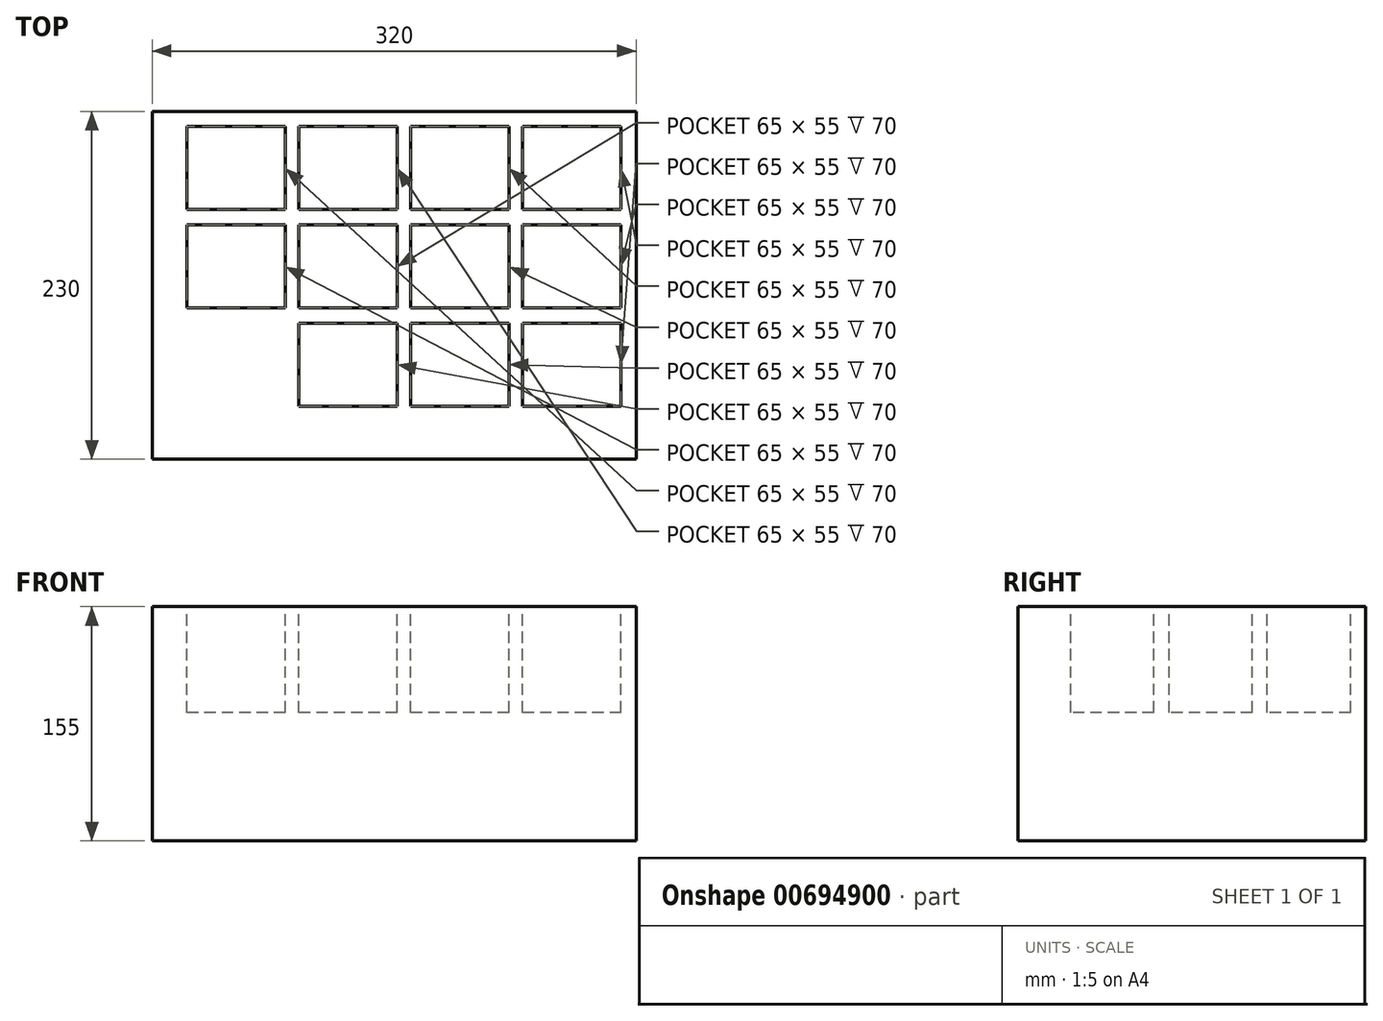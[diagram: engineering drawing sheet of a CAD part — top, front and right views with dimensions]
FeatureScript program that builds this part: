
annotation { "Feature Type Name" : "Feature", "Feature Type Description" : "" }
export const myFeature = defineFeature(function(context is Context, id is Id, definition is map)
    precondition{}
    {
        {
            var Q0;
            Q0=qCreatedBy(makeId("Top.planeOp"),FACE);
            var sketch = newSketch(context, id + "F0", { "sketchPlane" : qUnion([Q0])});
            skLineSegment(sketch, "E0.bottom", {"start": v(0, 0) * mm, "end": v(320, 0) * mm});
            skLineSegment(sketch, "E0.top", {"start": v(0, 230) * mm, "end": v(320, 230) * mm});
            skLineSegment(sketch, "E0.left", {"start": v(0, 0) * mm, "end": v(0, 230) * mm});
            skLineSegment(sketch, "E0.right", {"start": v(320, 0) * mm, "end": v(320, 230) * mm});
            skSolve(sketch);
        }
        {
            var Q0;
            Q0=makeQuery(id+"F0.imprint","IMPRINT",FACE,{"disambiguationData":[TD([[makeQuery(id+"F0.imprint","IMPRINT",EDGE,{"derivedFrom":sQuery(id+"F0.wireOp",EDGE,"E0.bottom")}),1.0]])]});
            extrude(context, id + "F1", {"entities" : qUnion([Q0]), "depth" : 155 * mm, "offsetDistance" : 25 * mm});
        }
        {
            var Q0;
            Q0=makeQuery(id+"F1.opExtrude","CAP_FACE",FACE,{"disambiguationData":[OSD([sQuery(id+"F0.wireOp",EDGE,"E0.bottom"),sQuery(id+"F0.wireOp",EDGE,"E0.top"),sQuery(id+"F0.wireOp",EDGE,"E0.left"),sQuery(id+"F0.wireOp",EDGE,"E0.right")])],"isStart":false});
            var sketch = newSketch(context, id + "F2", { "sketchPlane" : qUnion([Q0])});
            skLineSegment(sketch, "E1.bottom", {"start": v(320, 230) * mm, "end": v(310, 230) * mm});
            skLineSegment(sketch, "E1.top", {"start": v(320, 220) * mm, "end": v(310, 220) * mm});
            skLineSegment(sketch, "E1.left", {"start": v(320, 230) * mm, "end": v(320, 220) * mm});
            skLineSegment(sketch, "E1.right", {"start": v(310, 230) * mm, "end": v(310, 220) * mm});
            skLineSegment(sketch, "E2.bottom", {"start": v(310, 220) * mm, "end": v(245, 220) * mm});
            skLineSegment(sketch, "E2.top", {"start": v(310, 165) * mm, "end": v(245, 165) * mm});
            skLineSegment(sketch, "E2.left", {"start": v(310, 220) * mm, "end": v(310, 165) * mm});
            skLineSegment(sketch, "E2.right", {"start": v(245, 220) * mm, "end": v(245, 165) * mm});
            skLineSegment(sketch, "E3.0.1.0", {"start": v(310, 155) * mm, "end": v(245, 155) * mm});
            skLineSegment(sketch, "E3.0.1.1", {"start": v(245, 155) * mm, "end": v(245, 100) * mm});
            skLineSegment(sketch, "E3.0.1.2", {"start": v(310, 155) * mm, "end": v(310, 100) * mm});
            skLineSegment(sketch, "E3.0.1.3", {"start": v(310, 100) * mm, "end": v(245, 100) * mm});
            skLineSegment(sketch, "E3.0.2.0", {"start": v(310, 90) * mm, "end": v(245, 90) * mm});
            skLineSegment(sketch, "E3.0.2.1", {"start": v(245, 90) * mm, "end": v(245, 35) * mm});
            skLineSegment(sketch, "E3.0.2.2", {"start": v(310, 90) * mm, "end": v(310, 35) * mm});
            skLineSegment(sketch, "E3.0.2.3", {"start": v(310, 35) * mm, "end": v(245, 35) * mm});
            skLineSegment(sketch, "E3.1.0.0", {"start": v(236, 220) * mm, "end": v(171, 220) * mm});
            skLineSegment(sketch, "E3.1.0.1", {"start": v(171, 220) * mm, "end": v(171, 165) * mm});
            skLineSegment(sketch, "E3.1.0.2", {"start": v(236, 220) * mm, "end": v(236, 165) * mm});
            skLineSegment(sketch, "E3.1.0.3", {"start": v(236, 165) * mm, "end": v(171, 165) * mm});
            skLineSegment(sketch, "E3.1.1.0", {"start": v(236, 155) * mm, "end": v(171, 155) * mm});
            skLineSegment(sketch, "E3.1.1.1", {"start": v(171, 155) * mm, "end": v(171, 100) * mm});
            skLineSegment(sketch, "E3.1.1.2", {"start": v(236, 155) * mm, "end": v(236, 100) * mm});
            skLineSegment(sketch, "E3.1.1.3", {"start": v(236, 100) * mm, "end": v(171, 100) * mm});
            skLineSegment(sketch, "E3.1.2.0", {"start": v(236, 90) * mm, "end": v(171, 90) * mm});
            skLineSegment(sketch, "E3.1.2.1", {"start": v(171, 90) * mm, "end": v(171, 35) * mm});
            skLineSegment(sketch, "E3.1.2.2", {"start": v(236, 90) * mm, "end": v(236, 35) * mm});
            skLineSegment(sketch, "E3.1.2.3", {"start": v(236, 35) * mm, "end": v(171, 35) * mm});
            skLineSegment(sketch, "E3.2.0.0", {"start": v(162, 220) * mm, "end": v(97, 220) * mm});
            skLineSegment(sketch, "E3.2.0.1", {"start": v(97, 220) * mm, "end": v(97, 165) * mm});
            skLineSegment(sketch, "E3.2.0.2", {"start": v(162, 220) * mm, "end": v(162, 165) * mm});
            skLineSegment(sketch, "E3.2.0.3", {"start": v(162, 165) * mm, "end": v(97, 165) * mm});
            skLineSegment(sketch, "E3.2.1.0", {"start": v(162, 155) * mm, "end": v(97, 155) * mm});
            skLineSegment(sketch, "E3.2.1.1", {"start": v(97, 155) * mm, "end": v(97, 100) * mm});
            skLineSegment(sketch, "E3.2.1.2", {"start": v(162, 155) * mm, "end": v(162, 100) * mm});
            skLineSegment(sketch, "E3.2.1.3", {"start": v(162, 100) * mm, "end": v(97, 100) * mm});
            skLineSegment(sketch, "E3.2.2.0", {"start": v(162, 90) * mm, "end": v(97, 90) * mm});
            skLineSegment(sketch, "E3.2.2.1", {"start": v(97, 90) * mm, "end": v(97, 35) * mm});
            skLineSegment(sketch, "E3.2.2.2", {"start": v(162, 90) * mm, "end": v(162, 35) * mm});
            skLineSegment(sketch, "E3.2.2.3", {"start": v(162, 35) * mm, "end": v(97, 35) * mm});
            skLineSegment(sketch, "E3.3.0.0", {"start": v(88, 220) * mm, "end": v(23, 220) * mm});
            skLineSegment(sketch, "E3.3.0.1", {"start": v(23, 220) * mm, "end": v(23, 165) * mm});
            skLineSegment(sketch, "E3.3.0.2", {"start": v(88, 220) * mm, "end": v(88, 165) * mm});
            skLineSegment(sketch, "E3.3.0.3", {"start": v(88, 165) * mm, "end": v(23, 165) * mm});
            skLineSegment(sketch, "E3.3.1.0", {"start": v(88, 155) * mm, "end": v(23, 155) * mm});
            skLineSegment(sketch, "E3.3.1.1", {"start": v(23, 155) * mm, "end": v(23, 100) * mm});
            skLineSegment(sketch, "E3.3.1.2", {"start": v(88, 155) * mm, "end": v(88, 100) * mm});
            skLineSegment(sketch, "E3.3.1.3", {"start": v(88, 100) * mm, "end": v(23, 100) * mm});
            skLineSegment(sketch, "E3.3.2.0", {"start": v(88, 90) * mm, "end": v(23, 90) * mm});
            skLineSegment(sketch, "E3.3.2.1", {"start": v(23, 90) * mm, "end": v(23, 35) * mm});
            skLineSegment(sketch, "E3.3.2.2", {"start": v(88, 90) * mm, "end": v(88, 35) * mm});
            skLineSegment(sketch, "E3.3.2.3", {"start": v(88, 35) * mm, "end": v(23, 35) * mm});
            skLineSegment(sketch, "E3.direction1", {"start": v(245, 220) * mm, "end": v(171, 220) * mm, "construction": true});
            skLineSegment(sketch, "E3.direction2", {"start": v(245, 220) * mm, "end": v(245, 155) * mm, "construction": true});
            skSolve(sketch);
        }
        {
            var Q0;
            Q0=makeQuery(id+"F2.imprint","IMPRINT",FACE,{"disambiguationData":[TD([[makeQuery(id+"F2.imprint","IMPRINT",EDGE,{"derivedFrom":sQuery(id+"F2.wireOp",EDGE,"E3.2.1.0")}),1.0]])]});
            var Q1;
            Q1=makeQuery(id+"F2.imprint","IMPRINT",FACE,{"disambiguationData":[TD([[makeQuery(id+"F2.imprint","IMPRINT",EDGE,{"derivedFrom":sQuery(id+"F2.wireOp",EDGE,"E3.2.0.0")}),1.0]])]});
            var Q2;
            Q2=makeQuery(id+"F2.imprint","IMPRINT",FACE,{"disambiguationData":[TD([[makeQuery(id+"F2.imprint","IMPRINT",EDGE,{"derivedFrom":sQuery(id+"F2.wireOp",EDGE,"E3.3.0.0")}),1.0]])]});
            var Q3;
            Q3=makeQuery(id+"F2.imprint","IMPRINT",FACE,{"disambiguationData":[TD([[makeQuery(id+"F2.imprint","IMPRINT",EDGE,{"derivedFrom":sQuery(id+"F2.wireOp",EDGE,"E3.3.1.0")}),1.0]])]});
            var Q4;
            Q4=makeQuery(id+"F2.imprint","IMPRINT",FACE,{"disambiguationData":[TD([[makeQuery(id+"F2.imprint","IMPRINT",EDGE,{"derivedFrom":sQuery(id+"F2.wireOp",EDGE,"E3.2.2.0")}),1.0]])]});
            var Q5;
            Q5=makeQuery(id+"F2.imprint","IMPRINT",FACE,{"disambiguationData":[TD([[makeQuery(id+"F2.imprint","IMPRINT",EDGE,{"derivedFrom":sQuery(id+"F2.wireOp",EDGE,"E3.1.2.0")}),1.0]])]});
            var Q6;
            Q6=makeQuery(id+"F2.imprint","IMPRINT",FACE,{"disambiguationData":[TD([[makeQuery(id+"F2.imprint","IMPRINT",EDGE,{"derivedFrom":sQuery(id+"F2.wireOp",EDGE,"E3.1.1.0")}),1.0]])]});
            var Q7;
            Q7=makeQuery(id+"F2.imprint","IMPRINT",FACE,{"disambiguationData":[TD([[makeQuery(id+"F2.imprint","IMPRINT",EDGE,{"derivedFrom":sQuery(id+"F2.wireOp",EDGE,"E3.1.0.0")}),1.0]])]});
            var Q8;
            Q8=makeQuery(id+"F2.imprint","IMPRINT",FACE,{"disambiguationData":[TD([[makeQuery(id+"F2.imprint","IMPRINT",EDGE,{"derivedFrom":sQuery(id+"F2.wireOp",EDGE,"E2.bottom")}),1.0]])]});
            var Q9;
            Q9=makeQuery(id+"F2.imprint","IMPRINT",FACE,{"disambiguationData":[TD([[makeQuery(id+"F2.imprint","IMPRINT",EDGE,{"derivedFrom":sQuery(id+"F2.wireOp",EDGE,"E3.0.1.0")}),1.0]])]});
            var Q10;
            Q10=makeQuery(id+"F2.imprint","IMPRINT",FACE,{"disambiguationData":[TD([[makeQuery(id+"F2.imprint","IMPRINT",EDGE,{"derivedFrom":sQuery(id+"F2.wireOp",EDGE,"E3.0.2.0")}),1.0]])]});
            extrude(context, id + "F3", {"entities" : qUnion([Q0, Q1, Q2, Q3, Q4, Q5, Q6, Q7, Q8, Q9, Q10]), "operationType" : NewBodyOperationType.REMOVE, "oppositeDirection" : true, "depth" : 70 * mm, "offsetDistance" : 25 * mm});
        }
    });
